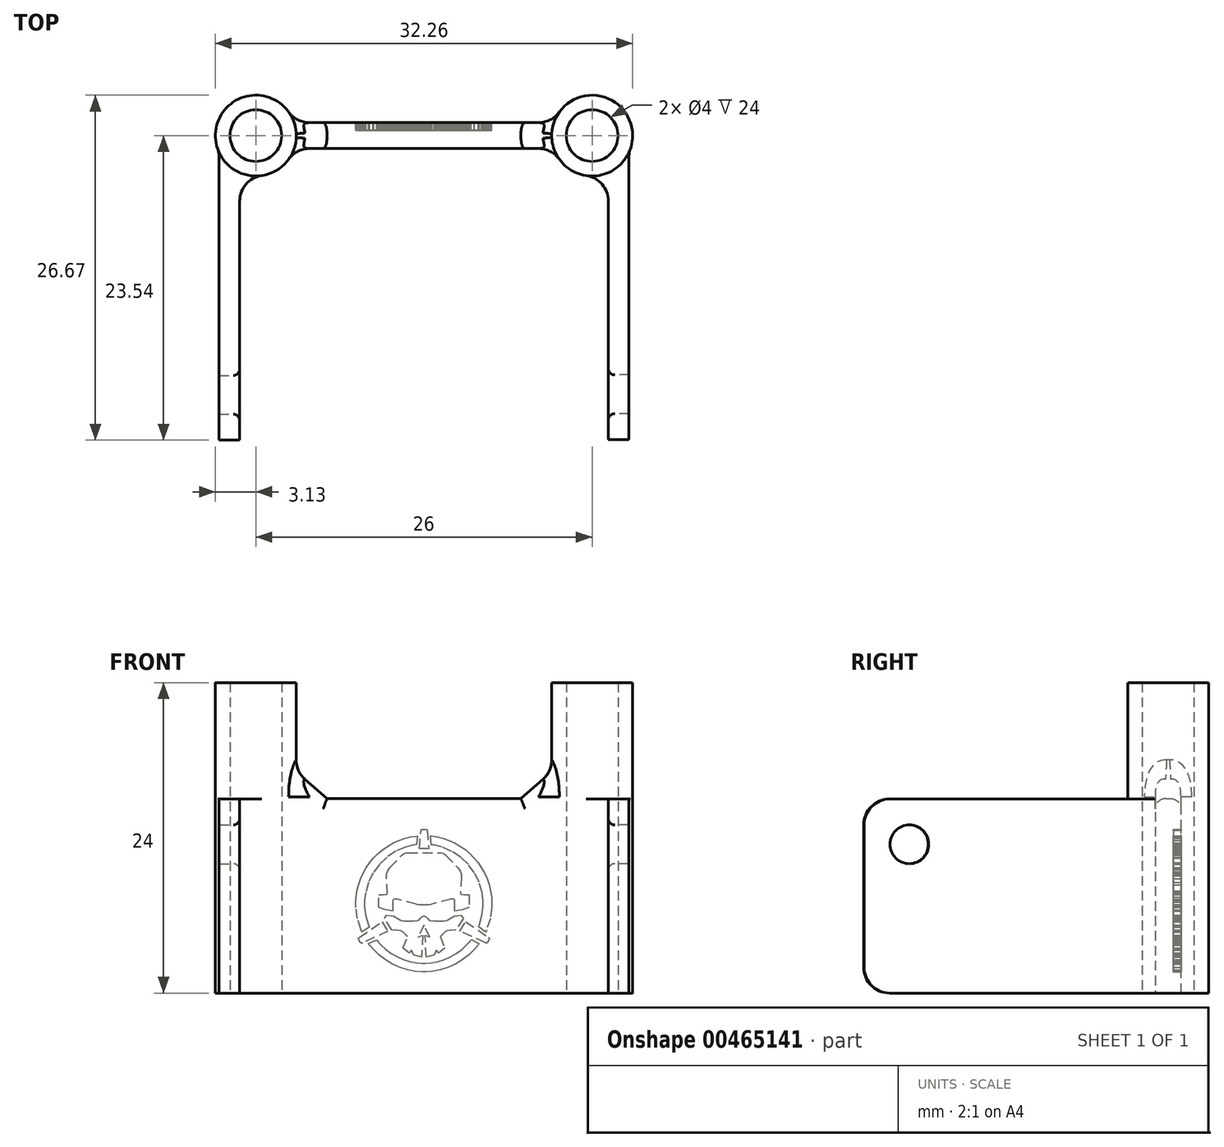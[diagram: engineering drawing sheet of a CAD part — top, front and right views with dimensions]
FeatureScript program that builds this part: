
annotation { "Feature Type Name" : "Feature", "Feature Type Description" : "" }
export const myFeature = defineFeature(function(context is Context, id is Id, definition is map)
    precondition{}
    {
        {
            var Q0;
            Q0=qCreatedBy(makeId("Top.planeOp"),FACE);
            var sketch = newSketch(context, id + "F0", { "sketchPlane" : qUnion([Q0])});
            skCircle(sketch, "E0", {"center": v(-13, 0) * mm, "radius": 3.12 * mm});
            skCircle(sketch, "E1", {"center": v(13, 0) * mm, "radius": 3.12 * mm});
            skSolve(sketch);
        }
        {
            var Q0;
            Q0 = qSketchRegion(id + "F0", true);
            extrude(context, id + "F1", {"entities" : qUnion([Q0]), "depth" : 24 * mm});
        }
        {
            var Q0;
            Q0=qCreatedBy(makeId("Front.planeOp"),FACE);
            var sketch = newSketch(context, id + "F2", { "sketchPlane" : qUnion([Q0])});
            skLineSegment(sketch, "E2", {"start": v(12, 0) * mm, "end": v(12, 19) * mm});
            skLineSegment(sketch, "E3", {"start": v(12, 19) * mm, "end": v(12, 19) * mm});
            skLineSegment(sketch, "E4", {"start": v(12, 19) * mm, "end": v(7.5, 15.03) * mm});
            skLineSegment(sketch, "E5", {"start": v(7.5, 15.03) * mm, "end": v(-7.5, 15.03) * mm});
            skLineSegment(sketch, "E6", {"start": v(-7.5, 15.03) * mm, "end": v(-12, 19) * mm});
            skLineSegment(sketch, "E7", {"start": v(-12, 19) * mm, "end": v(-12, 0) * mm});
            skLineSegment(sketch, "E8", {"start": v(-12, 0) * mm, "end": v(12, 0) * mm});
            skSolve(sketch);
        }
        {
            var Q0;
            Q0=makeQuery(id+"F2.imprint","IMPRINT",FACE,{"disambiguationData":[TD([[makeQuery(id+"F2.imprint","IMPRINT",EDGE,{"derivedFrom":sQuery(id+"F2.wireOp",EDGE,"E2")}),1.0]])]});
            extrude(context, id + "F3", {"entities" : qUnion([Q0]), "endBound" : BoundingType.SYMMETRIC, "depth" : 2 * mm});
        }
        {
            var Q0;
            Q0=qCreatedBy(makeId("Right.planeOp"),FACE);
            var Q1;
            Q1 = qBodyType(qCreatedBy(id + "F5" ,EDGE), BodyType.WIRE);
            cPlane(context, id + "F4", {"entities" : qUnion([Q0, Q1]), "cplaneType" : CPlaneType.OFFSET, "offset" : 14.25 * mm, "width" : 150 * mm, "height" : 150 * mm});
        }
        {
            var Q0;
            Q0=qCreatedBy(id+"F4.planeOp",FACE);
            var sketch = newSketch(context, id + "F5", { "sketchPlane" : qUnion([Q0])});
            skCircle(sketch, "E9", {"center": v(-20, 11.5) * mm, "radius": 1.5 * mm});
            skLineSegment(sketch, "E10", {"start": v(0, 0) * mm, "end": v(-21.5, 0) * mm});
            skLineSegment(sketch, "E11", {"start": v(-23.5, 2) * mm, "end": v(-23.5, 13) * mm});
            skLineSegment(sketch, "E12", {"start": v(-21.5, 15) * mm, "end": v(0, 15) * mm});
            skLineSegment(sketch, "E13", {"start": v(0, 15) * mm, "end": v(0, 0) * mm});
            skPoint(sketch, "E14.visualSharp", {"position": v(-23.5, 15) * mm});
            skArc(sketch, "E14.filletArc", {"start": v(-21.5, 15) * mm, "mid": v(-22.91, 14.41) * mm, "end": v(-23.5, 13) * mm});
            skPoint(sketch, "E15.visualSharp", {"position": v(-23.5, 0) * mm});
            skArc(sketch, "E15.filletArc", {"start": v(-23.5, 2) * mm, "mid": v(-22.91, 0.59) * mm, "end": v(-21.5, 0) * mm});
            skSolve(sketch);
        }
        {
            var Q0;
            Q0 = qSketchRegion(id + "F5", true);
            extrude(context, id + "F6", {"entities" : qUnion([Q0]), "operationType" : NewBodyOperationType.ADD, "depth" : 1.6 * mm});
        }
        {
            var Q0;
            Q0=qCreatedBy(makeId("Right.planeOp"),FACE);
            cPlane(context, id + "F7", {"entities" : qUnion([Q0]), "cplaneType" : CPlaneType.OFFSET, "offset" : 14.25 * mm, "oppositeDirection" : true, "width" : 150 * mm, "height" : 150 * mm});
        }
        {
            var Q0;
            Q0=qCreatedBy(id+"F7.planeOp",FACE);
            var sketch = newSketch(context, id + "F8", { "sketchPlane" : qUnion([Q0])});
            skCircle(sketch, "E16", {"center": v(-20.04, 11.5) * mm, "radius": 1.5 * mm});
            skLineSegment(sketch, "E17", {"start": v(-0.04, 0) * mm, "end": v(-21.54, 0) * mm});
            skLineSegment(sketch, "E18", {"start": v(-23.54, 2) * mm, "end": v(-23.54, 13) * mm});
            skLineSegment(sketch, "E19", {"start": v(-21.54, 15) * mm, "end": v(-0.04, 15) * mm});
            skLineSegment(sketch, "E20", {"start": v(-0.04, 15) * mm, "end": v(-0.04, 0) * mm});
            skPoint(sketch, "E21.visualSharp", {"position": v(-23.54, 15) * mm});
            skArc(sketch, "E21.filletArc", {"start": v(-21.54, 15) * mm, "mid": v(-22.95, 14.41) * mm, "end": v(-23.54, 13) * mm});
            skPoint(sketch, "E22.visualSharp", {"position": v(-23.54, 0) * mm});
            skArc(sketch, "E22.filletArc", {"start": v(-23.54, 2) * mm, "mid": v(-22.95, 0.59) * mm, "end": v(-21.54, 0) * mm});
            skSolve(sketch);
        }
        {
            var Q0;
            Q0 = qSketchRegion(id + "F8", true);
            extrude(context, id + "F9", {"entities" : qUnion([Q0]), "operationType" : NewBodyOperationType.ADD, "oppositeDirection" : true, "depth" : 1.6 * mm});
        }
        {
            var Q0;
            Q0=qCreatedBy(makeId("Top.planeOp"),FACE);
            var sketch = newSketch(context, id + "F10", { "sketchPlane" : qUnion([Q0])});
            skCircle(sketch, "E23", {"center": v(-13, 0) * mm, "radius": 0.5 * mm});
            skCircle(sketch, "E24", {"center": v(13, 0) * mm, "radius": 1.75 * mm});
            skSolve(sketch);
        }
        {
            var Q0;
            Q0=sQuery(id+"F10.wireOp",VERTEX,"E23.center");
            var Q1;
            Q1=sQuery(id+"F10.wireOp",VERTEX,"E24.center");
            var Q2;
            Q2=makeQuery(id+"F1.opExtrude","SWEPT_BODY",BODY,{"disambiguationData":[OSD([sQuery(id+"F0.wireOp",EDGE,"E0")])]});
            var Q3;
            Q3=makeQuery(id+"F3.opExtrude","SWEPT_BODY",BODY,{"disambiguationData":[OSD([sQuery(id+"F2.wireOp",EDGE,"in345Lub-D59E-tOme-60dj-Cq3KucnByxKd"),sQuery(id+"F2.wireOp",EDGE,"E2"),sQuery(id+"F2.wireOp",EDGE,"E4"),sQuery(id+"F2.wireOp",EDGE,"E5"),sQuery(id+"F2.wireOp",EDGE,"E6"),sQuery(id+"F2.wireOp",EDGE,"E7")])]});
            var Q4;
            Q4=makeQuery(id+"FYRTTrcSvXfLMjP_3.opExtrude","SWEPT_BODY",BODY,{"disambiguationData":[OSD([sQuery(id+"Fs8EBPNxBlUYa75_3.wireOp",EDGE,"JWLeMf17-8jiZ-tYXv-UtJK-ccR32AaEOkmf.bottom"),sQuery(id+"Fs8EBPNxBlUYa75_3.wireOp",EDGE,"JWLeMf17-8jiZ-tYXv-UtJK-ccR32AaEOkmf.top"),sQuery(id+"Fs8EBPNxBlUYa75_3.wireOp",EDGE,"JWLeMf17-8jiZ-tYXv-UtJK-ccR32AaEOkmf.left"),sQuery(id+"Fs8EBPNxBlUYa75_3.wireOp",EDGE,"JWLeMf17-8jiZ-tYXv-UtJK-ccR32AaEOkmf.right")])]});
            var Q5;
            Q5=makeQuery(id+"F1.opExtrude","SWEPT_BODY",BODY,{"disambiguationData":[OSD([sQuery(id+"F0.wireOp",EDGE,"E1")])]});
            var Q6;
            Q6=makeQuery(id+"FYRTTrcSvXfLMjP_3.opExtrude","SWEPT_BODY",BODY,{"disambiguationData":[OSD([sQuery(id+"Fs8EBPNxBlUYa75_3.wireOp",EDGE,"dHJZYZbQ-VqZX-6sAW-GdeU-ZCC2gI22Ho79.bottom"),sQuery(id+"Fs8EBPNxBlUYa75_3.wireOp",EDGE,"dHJZYZbQ-VqZX-6sAW-GdeU-ZCC2gI22Ho79.top"),sQuery(id+"Fs8EBPNxBlUYa75_3.wireOp",EDGE,"dHJZYZbQ-VqZX-6sAW-GdeU-ZCC2gI22Ho79.left"),sQuery(id+"Fs8EBPNxBlUYa75_3.wireOp",EDGE,"dHJZYZbQ-VqZX-6sAW-GdeU-ZCC2gI22Ho79.right")])]});
            hole(context, id + "F11", {"style" : HoleStyle.SIMPLE, "endStyle" : HoleEndStyle.THROUGH, "oppositeDirection" : true, "holeDiameter" : 4 * mm, "isTappedThrough" : true, "tappedDepth" : 12 * mm, "tapClearance" : 3, "locations" : qUnion([Q0, Q1]), "scope" : qUnion([Q2, Q3, Q4, Q5, Q6])});
        }
        {
            var Q0;
            Q0=makeQuery(id+"F1.opExtrude","SWEPT_BODY",BODY,{"disambiguationData":[OSD([sQuery(id+"F0.wireOp",EDGE,"E1")])]});
            var Q1;
            Q1=makeQuery(id+"F3.opExtrude","SWEPT_BODY",BODY,{"disambiguationData":[OSD([sQuery(id+"F2.wireOp",EDGE,"in345Lub-D59E-tOme-60dj-Cq3KucnByxKd"),sQuery(id+"F2.wireOp",EDGE,"E2"),sQuery(id+"F2.wireOp",EDGE,"E4"),sQuery(id+"F2.wireOp",EDGE,"E5"),sQuery(id+"F2.wireOp",EDGE,"E6"),sQuery(id+"F2.wireOp",EDGE,"E7")])]});
            var Q2;
            Q2=makeQuery(id+"F1.opExtrude","SWEPT_BODY",BODY,{"disambiguationData":[OSD([sQuery(id+"F0.wireOp",EDGE,"E0")])]});
            booleanBodies(context, id + "F12", {"operationType" : BooleanOperationType.UNION, "tools" : qUnion([Q0, Q1, Q2])});
        }
        {
            var Q0;
            Q0=makeQuery(id+"F3.opExtrude","CAP_EDGE",EDGE,{"disambiguationData":[OSD([sQuery(id+"F2.wireOp",EDGE,"E5")])],"isStart":false});
            var Q1;
            Q1=makeQuery(id+"F3.opExtrude","CAP_EDGE",EDGE,{"disambiguationData":[OSD([sQuery(id+"F2.wireOp",EDGE,"E5")])],"isStart":true});
            var Q2;
            Q2=makeQuery(id+"F3.opExtrude","CAP_EDGE",EDGE,{"disambiguationData":[OSD([sQuery(id+"F2.wireOp",EDGE,"E6")])],"isStart":false});
            var Q3;
            Q3=makeQuery(id+"F3.opExtrude","CAP_EDGE",EDGE,{"disambiguationData":[OSD([sQuery(id+"F2.wireOp",EDGE,"E6")])],"isStart":true});
            var Q4;
            Q4=makeQuery(id+"F3.opExtrude","CAP_EDGE",EDGE,{"disambiguationData":[OSD([sQuery(id+"F2.wireOp",EDGE,"E4")])],"isStart":false});
            var Q5;
            Q5=makeQuery(id+"F3.opExtrude","CAP_EDGE",EDGE,{"disambiguationData":[OSD([sQuery(id+"F2.wireOp",EDGE,"E4")])],"isStart":true});
            fillet(context, id + "F13", {"entities" : qUnion([Q0, Q1, Q2, Q3, Q4, Q5]), "radius" : .8 * mm, "tangentPropagation" : true, "allowEdgeOverflow" : false});
        }
        {
            var Q0;
            Q0=makeQuery(id+"F11.hole-0.boolean.opBoolean","INTERSECT",EDGE,{"derivedFrom":[makeQuery(id+"F1.opExtrude","CAP_FACE",FACE,{"disambiguationData":[OSD([sQuery(id+"F0.wireOp",EDGE,"E0")])],"isStart":false}),makeQuery(id+"F11.hole-0.opRevolve","SWEPT_FACE",FACE,{"disambiguationData":[OSD([sQuery(id+"F11.hole-0.sketch.wireOp",EDGE,"core_line_2")])]})]});
            var Q1;
            Q1=makeQuery(id+"F11.hole-1.boolean.opBoolean","INTERSECT",EDGE,{"derivedFrom":[makeQuery(id+"F1.opExtrude","CAP_FACE",FACE,{"disambiguationData":[OSD([sQuery(id+"F0.wireOp",EDGE,"E1")])],"isStart":false}),makeQuery(id+"F11.hole-1.opRevolve","SWEPT_FACE",FACE,{"disambiguationData":[OSD([sQuery(id+"F11.hole-1.sketch.wireOp",EDGE,"core_line_2")])]})]});
            var Q2;
            Q2=makeQuery(id+"F9.opExtrude","CAP_EDGE",EDGE,{"disambiguationData":[OSD([sQuery(id+"F8.wireOp",EDGE,"E16")])],"isStart":true});
            var Q3;
            Q3=makeQuery(id+"F6.opExtrude","CAP_EDGE",EDGE,{"disambiguationData":[OSD([sQuery(id+"F5.wireOp",EDGE,"E9")])],"isStart":true});
            fillet(context, id + "F14", {"entities" : qUnion([Q0, Q1, Q2, Q3]), "radius" : .5 * mm, "tangentPropagation" : true, "allowEdgeOverflow" : false});
        }
        {
            var Q0;
            Q0=makeQuery(id+"F3.opExtrude","CAP_FACE",FACE,{"disambiguationData":[OSD([sQuery(id+"F2.wireOp",EDGE,"E2"),sQuery(id+"F2.wireOp",EDGE,"E4"),sQuery(id+"F2.wireOp",EDGE,"E5"),sQuery(id+"F2.wireOp",EDGE,"E6"),sQuery(id+"F2.wireOp",EDGE,"E7"),sQuery(id+"F2.wireOp",EDGE,"E8")])],"isStart":true});
            var sketch = newSketch(context, id + "F15", { "sketchPlane" : qUnion([Q0])});
            skLineSegment(sketch, "E25", {"start": v(-0.2, 12.65) * mm, "end": v(-0.2, 12.64) * mm});
            skLineSegment(sketch, "E26", {"start": v(-0.2, 12.64) * mm, "end": v(-0.23, 12.63) * mm});
            skLineSegment(sketch, "E27", {"start": v(-0.23, 12.63) * mm, "end": v(-0.24, 12.59) * mm});
            skLineSegment(sketch, "E28", {"start": v(-0.24, 12.59) * mm, "end": v(-0.24, 12.58) * mm});
            skLineSegment(sketch, "E29", {"start": v(-0.24, 12.58) * mm, "end": v(-0.38, 11.17) * mm});
            skLineSegment(sketch, "E30", {"start": v(-0.38, 11.17) * mm, "end": v(0.36, 11.17) * mm});
            skLineSegment(sketch, "E31", {"start": v(0.36, 11.17) * mm, "end": v(0.22, 12.58) * mm});
            skLineSegment(sketch, "E32", {"start": v(0.22, 12.58) * mm, "end": v(0.22, 12.59) * mm});
            skLineSegment(sketch, "E33", {"start": v(0.22, 12.59) * mm, "end": v(0.2, 12.63) * mm});
            skLineSegment(sketch, "E34", {"start": v(0.2, 12.63) * mm, "end": v(0.19, 12.64) * mm});
            skLineSegment(sketch, "E35", {"start": v(0.19, 12.64) * mm, "end": v(0.18, 12.65) * mm});
            skLineSegment(sketch, "E36", {"start": v(0.18, 12.65) * mm, "end": v(-0.2, 12.65) * mm});
            skLineSegment(sketch, "E37", {"start": v(-0.5, 12.15) * mm, "end": v(-0.63, 12.13) * mm});
            skLineSegment(sketch, "E38", {"start": v(-0.63, 12.13) * mm, "end": v(-1, 12.07) * mm});
            skLineSegment(sketch, "E39", {"start": v(-1, 12.07) * mm, "end": v(-1.48, 11.96) * mm});
            skLineSegment(sketch, "E40", {"start": v(-1.48, 11.96) * mm, "end": v(-1.94, 11.8) * mm});
            skLineSegment(sketch, "E41", {"start": v(-1.94, 11.8) * mm, "end": v(-2.38, 11.6) * mm});
            skLineSegment(sketch, "E42", {"start": v(-2.38, 11.6) * mm, "end": v(-2.8, 11.36) * mm});
            skLineSegment(sketch, "E43", {"start": v(-2.8, 11.36) * mm, "end": v(-3.19, 11.09) * mm});
            skLineSegment(sketch, "E44", {"start": v(-3.19, 11.09) * mm, "end": v(-3.55, 10.78) * mm});
            skLineSegment(sketch, "E45", {"start": v(-3.55, 10.78) * mm, "end": v(-3.89, 10.44) * mm});
            skLineSegment(sketch, "E46", {"start": v(-3.89, 10.44) * mm, "end": v(-4.19, 10.08) * mm});
            skLineSegment(sketch, "E47", {"start": v(-4.19, 10.08) * mm, "end": v(-4.46, 9.69) * mm});
            skLineSegment(sketch, "E48", {"start": v(-4.46, 9.69) * mm, "end": v(-4.69, 9.27) * mm});
            skLineSegment(sketch, "E49", {"start": v(-4.69, 9.27) * mm, "end": v(-4.88, 8.83) * mm});
            skLineSegment(sketch, "E50", {"start": v(-4.88, 8.83) * mm, "end": v(-5.04, 8.38) * mm});
            skLineSegment(sketch, "E51", {"start": v(-5.04, 8.38) * mm, "end": v(-5.15, 7.9) * mm});
            skLineSegment(sketch, "E52", {"start": v(-5.15, 7.9) * mm, "end": v(-5.22, 7.41) * mm});
            skLineSegment(sketch, "E53", {"start": v(-5.22, 7.41) * mm, "end": v(-5.25, 7.04) * mm});
            skLineSegment(sketch, "E54", {"start": v(-5.25, 7.04) * mm, "end": v(-5.25, 6.9) * mm});
            skLineSegment(sketch, "E55", {"start": v(-5.25, 6.9) * mm, "end": v(-5.25, 6.63) * mm});
            skLineSegment(sketch, "E56", {"start": v(-5.25, 6.63) * mm, "end": v(-5.12, 5.77) * mm});
            skLineSegment(sketch, "E57", {"start": v(-5.12, 5.77) * mm, "end": v(-4.85, 4.89) * mm});
            skLineSegment(sketch, "E58", {"start": v(-4.85, 4.89) * mm, "end": v(-4.77, 4.72) * mm});
            skLineSegment(sketch, "E59", {"start": v(-4.77, 4.72) * mm, "end": v(-4.22, 5.12) * mm});
            skLineSegment(sketch, "E60", {"start": v(-4.22, 5.12) * mm, "end": v(-4.28, 5.25) * mm});
            skLineSegment(sketch, "E61", {"start": v(-4.28, 5.25) * mm, "end": v(-4.49, 5.98) * mm});
            skLineSegment(sketch, "E62", {"start": v(-4.49, 5.98) * mm, "end": v(-4.58, 6.68) * mm});
            skLineSegment(sketch, "E63", {"start": v(-4.58, 6.68) * mm, "end": v(-4.58, 6.9) * mm});
            skLineSegment(sketch, "E64", {"start": v(-4.58, 6.9) * mm, "end": v(-4.58, 7.12) * mm});
            skLineSegment(sketch, "E65", {"start": v(-4.58, 7.12) * mm, "end": v(-4.5, 7.76) * mm});
            skLineSegment(sketch, "E66", {"start": v(-4.5, 7.76) * mm, "end": v(-4.28, 8.56) * mm});
            skLineSegment(sketch, "E67", {"start": v(-4.28, 8.56) * mm, "end": v(-3.91, 9.3) * mm});
            skLineSegment(sketch, "E68", {"start": v(-3.91, 9.3) * mm, "end": v(-3.43, 9.95) * mm});
            skLineSegment(sketch, "E69", {"start": v(-3.43, 9.95) * mm, "end": v(-2.84, 10.5) * mm});
            skLineSegment(sketch, "E70", {"start": v(-2.84, 10.5) * mm, "end": v(-2.16, 10.96) * mm});
            skLineSegment(sketch, "E71", {"start": v(-2.16, 10.96) * mm, "end": v(-1.4, 11.28) * mm});
            skLineSegment(sketch, "E72", {"start": v(-1.4, 11.28) * mm, "end": v(-0.78, 11.44) * mm});
            skLineSegment(sketch, "E73", {"start": v(-0.78, 11.44) * mm, "end": v(-0.57, 11.46) * mm});
            skLineSegment(sketch, "E74", {"start": v(-0.57, 11.46) * mm, "end": v(-0.5, 12.15) * mm});
            skLineSegment(sketch, "E75", {"start": v(0.52, 12.14) * mm, "end": v(0.58, 11.47) * mm});
            skLineSegment(sketch, "E76", {"start": v(0.58, 11.47) * mm, "end": v(0.79, 11.44) * mm});
            skLineSegment(sketch, "E77", {"start": v(0.79, 11.44) * mm, "end": v(1.4, 11.28) * mm});
            skLineSegment(sketch, "E78", {"start": v(1.4, 11.28) * mm, "end": v(2.17, 10.96) * mm});
            skLineSegment(sketch, "E79", {"start": v(2.17, 10.96) * mm, "end": v(2.86, 10.5) * mm});
            skLineSegment(sketch, "E80", {"start": v(2.86, 10.5) * mm, "end": v(3.45, 9.95) * mm});
            skLineSegment(sketch, "E81", {"start": v(3.45, 9.95) * mm, "end": v(3.93, 9.3) * mm});
            skLineSegment(sketch, "E82", {"start": v(3.93, 9.3) * mm, "end": v(4.3, 8.56) * mm});
            skLineSegment(sketch, "E83", {"start": v(4.3, 8.56) * mm, "end": v(4.52, 7.76) * mm});
            skLineSegment(sketch, "E84", {"start": v(4.52, 7.76) * mm, "end": v(4.6, 7.12) * mm});
            skLineSegment(sketch, "E85", {"start": v(4.6, 7.12) * mm, "end": v(4.6, 6.9) * mm});
            skLineSegment(sketch, "E86", {"start": v(4.6, 6.9) * mm, "end": v(4.6, 6.68) * mm});
            skLineSegment(sketch, "E87", {"start": v(4.6, 6.68) * mm, "end": v(4.5, 5.98) * mm});
            skLineSegment(sketch, "E88", {"start": v(4.5, 5.98) * mm, "end": v(4.3, 5.25) * mm});
            skLineSegment(sketch, "E89", {"start": v(4.3, 5.25) * mm, "end": v(4.23, 5.11) * mm});
            skLineSegment(sketch, "E90", {"start": v(4.23, 5.11) * mm, "end": v(4.78, 4.71) * mm});
            skLineSegment(sketch, "E91", {"start": v(4.78, 4.71) * mm, "end": v(4.86, 4.88) * mm});
            skLineSegment(sketch, "E92", {"start": v(4.86, 4.88) * mm, "end": v(5.14, 5.77) * mm});
            skLineSegment(sketch, "E93", {"start": v(5.14, 5.77) * mm, "end": v(5.26, 6.62) * mm});
            skLineSegment(sketch, "E94", {"start": v(5.26, 6.62) * mm, "end": v(5.26, 6.9) * mm});
            skLineSegment(sketch, "E95", {"start": v(5.26, 6.9) * mm, "end": v(5.26, 7.04) * mm});
            skLineSegment(sketch, "E96", {"start": v(5.26, 7.04) * mm, "end": v(5.24, 7.41) * mm});
            skLineSegment(sketch, "E97", {"start": v(5.24, 7.41) * mm, "end": v(5.17, 7.9) * mm});
            skLineSegment(sketch, "E98", {"start": v(5.17, 7.9) * mm, "end": v(5.05, 8.37) * mm});
            skLineSegment(sketch, "E99", {"start": v(5.05, 8.37) * mm, "end": v(4.9, 8.83) * mm});
            skLineSegment(sketch, "E100", {"start": v(4.9, 8.83) * mm, "end": v(4.7, 9.27) * mm});
            skLineSegment(sketch, "E101", {"start": v(4.7, 9.27) * mm, "end": v(4.47, 9.68) * mm});
            skLineSegment(sketch, "E102", {"start": v(4.47, 9.68) * mm, "end": v(4.2, 10.08) * mm});
            skLineSegment(sketch, "E103", {"start": v(4.2, 10.08) * mm, "end": v(3.9, 10.44) * mm});
            skLineSegment(sketch, "E104", {"start": v(3.9, 10.44) * mm, "end": v(3.56, 10.78) * mm});
            skLineSegment(sketch, "E105", {"start": v(3.56, 10.78) * mm, "end": v(3.2, 11.08) * mm});
            skLineSegment(sketch, "E106", {"start": v(3.2, 11.08) * mm, "end": v(2.8, 11.36) * mm});
            skLineSegment(sketch, "E107", {"start": v(2.8, 11.36) * mm, "end": v(2.4, 11.6) * mm});
            skLineSegment(sketch, "E108", {"start": v(2.4, 11.6) * mm, "end": v(1.95, 11.8) * mm});
            skLineSegment(sketch, "E109", {"start": v(1.95, 11.8) * mm, "end": v(1.5, 11.95) * mm});
            skLineSegment(sketch, "E110", {"start": v(1.5, 11.95) * mm, "end": v(1.01, 12.07) * mm});
            skLineSegment(sketch, "E111", {"start": v(1.01, 12.07) * mm, "end": v(0.64, 12.13) * mm});
            skLineSegment(sketch, "E112", {"start": v(0.64, 12.13) * mm, "end": v(0.52, 12.14) * mm});
            skLineSegment(sketch, "E113", {"start": v(-1.2, 10.86) * mm, "end": v(-1.23, 10.86) * mm});
            skLineSegment(sketch, "E114", {"start": v(-1.23, 10.86) * mm, "end": v(-1.34, 10.84) * mm});
            skLineSegment(sketch, "E115", {"start": v(-1.34, 10.84) * mm, "end": v(-1.47, 10.8) * mm});
            skLineSegment(sketch, "E116", {"start": v(-1.47, 10.8) * mm, "end": v(-1.59, 10.75) * mm});
            skLineSegment(sketch, "E117", {"start": v(-1.59, 10.75) * mm, "end": v(-1.66, 10.69) * mm});
            skLineSegment(sketch, "E118", {"start": v(-1.66, 10.69) * mm, "end": v(-1.69, 10.66) * mm});
            skLineSegment(sketch, "E119", {"start": v(-1.69, 10.66) * mm, "end": v(-2.61, 9.7) * mm});
            skLineSegment(sketch, "E120", {"start": v(-2.61, 9.7) * mm, "end": v(-2.64, 9.67) * mm});
            skLineSegment(sketch, "E121", {"start": v(-2.64, 9.67) * mm, "end": v(-2.72, 9.56) * mm});
            skLineSegment(sketch, "E122", {"start": v(-2.72, 9.56) * mm, "end": v(-2.81, 9.39) * mm});
            skLineSegment(sketch, "E123", {"start": v(-2.81, 9.39) * mm, "end": v(-2.87, 9.2) * mm});
            skLineSegment(sketch, "E124", {"start": v(-2.87, 9.2) * mm, "end": v(-2.9, 9.05) * mm});
            skLineSegment(sketch, "E125", {"start": v(-2.9, 9.05) * mm, "end": v(-2.9, 9) * mm});
            skLineSegment(sketch, "E126", {"start": v(-2.9, 9) * mm, "end": v(-2.82, 7.67) * mm});
            skLineSegment(sketch, "E127", {"start": v(-2.82, 7.67) * mm, "end": v(-2.87, 7.65) * mm});
            skLineSegment(sketch, "E128", {"start": v(-2.87, 7.65) * mm, "end": v(-3.14, 7.6) * mm});
            skLineSegment(sketch, "E129", {"start": v(-3.14, 7.6) * mm, "end": v(-3.42, 7.6) * mm});
            skLineSegment(sketch, "E130", {"start": v(-3.42, 7.6) * mm, "end": v(-3.48, 7.6) * mm});
            skLineSegment(sketch, "E131", {"start": v(-3.48, 7.6) * mm, "end": v(-3.48, 6.61) * mm});
            skLineSegment(sketch, "E132", {"start": v(-3.48, 6.61) * mm, "end": v(-2.94, 6.42) * mm});
            skLineSegment(sketch, "E133", {"start": v(-2.94, 6.42) * mm, "end": v(-2.4, 6.35) * mm});
            skLineSegment(sketch, "E134", {"start": v(-2.4, 6.35) * mm, "end": v(-2.4, 7.11) * mm});
            skLineSegment(sketch, "E135", {"start": v(-2.4, 7.11) * mm, "end": v(-2.4, 7.13) * mm});
            skLineSegment(sketch, "E136", {"start": v(-2.4, 7.13) * mm, "end": v(-2.37, 7.2) * mm});
            skLineSegment(sketch, "E137", {"start": v(-2.37, 7.2) * mm, "end": v(-2.31, 7.25) * mm});
            skLineSegment(sketch, "E138", {"start": v(-2.31, 7.25) * mm, "end": v(-2.21, 7.27) * mm});
            skLineSegment(sketch, "E139", {"start": v(-2.21, 7.27) * mm, "end": v(-2.1, 7.27) * mm});
            skLineSegment(sketch, "E140", {"start": v(-2.1, 7.27) * mm, "end": v(-2.07, 7.26) * mm});
            skLineSegment(sketch, "E141", {"start": v(-2.07, 7.26) * mm, "end": v(-0.6, 6.87) * mm});
            skLineSegment(sketch, "E142", {"start": v(-0.6, 6.87) * mm, "end": v(-0.57, 6.86) * mm});
            skLineSegment(sketch, "E143", {"start": v(-0.57, 6.86) * mm, "end": v(-0.4, 6.82) * mm});
            skLineSegment(sketch, "E144", {"start": v(-0.4, 6.82) * mm, "end": v(-0.27, 6.8) * mm});
            skLineSegment(sketch, "E145", {"start": v(-0.27, 6.8) * mm, "end": v(-0.23, 6.8) * mm});
            skLineSegment(sketch, "E146", {"start": v(-0.23, 6.8) * mm, "end": v(0.24, 6.8) * mm});
            skLineSegment(sketch, "E147", {"start": v(0.24, 6.8) * mm, "end": v(0.29, 6.8) * mm});
            skLineSegment(sketch, "E148", {"start": v(0.29, 6.8) * mm, "end": v(0.42, 6.82) * mm});
            skLineSegment(sketch, "E149", {"start": v(0.42, 6.82) * mm, "end": v(0.58, 6.86) * mm});
            skLineSegment(sketch, "E150", {"start": v(0.58, 6.86) * mm, "end": v(0.61, 6.87) * mm});
            skLineSegment(sketch, "E151", {"start": v(0.61, 6.87) * mm, "end": v(2.08, 7.26) * mm});
            skLineSegment(sketch, "E152", {"start": v(2.08, 7.26) * mm, "end": v(2.12, 7.27) * mm});
            skLineSegment(sketch, "E153", {"start": v(2.12, 7.27) * mm, "end": v(2.23, 7.27) * mm});
            skLineSegment(sketch, "E154", {"start": v(2.23, 7.27) * mm, "end": v(2.33, 7.25) * mm});
            skLineSegment(sketch, "E155", {"start": v(2.33, 7.25) * mm, "end": v(2.39, 7.2) * mm});
            skLineSegment(sketch, "E156", {"start": v(2.39, 7.2) * mm, "end": v(2.4, 7.13) * mm});
            skLineSegment(sketch, "E157", {"start": v(2.4, 7.13) * mm, "end": v(2.4, 7.11) * mm});
            skLineSegment(sketch, "E158", {"start": v(2.4, 7.11) * mm, "end": v(2.4, 6.35) * mm});
            skLineSegment(sketch, "E159", {"start": v(2.4, 6.35) * mm, "end": v(2.96, 6.42) * mm});
            skLineSegment(sketch, "E160", {"start": v(2.96, 6.42) * mm, "end": v(3.5, 6.61) * mm});
            skLineSegment(sketch, "E161", {"start": v(3.5, 6.61) * mm, "end": v(3.5, 7.6) * mm});
            skLineSegment(sketch, "E162", {"start": v(3.5, 7.6) * mm, "end": v(3.44, 7.6) * mm});
            skLineSegment(sketch, "E163", {"start": v(3.44, 7.6) * mm, "end": v(3.16, 7.6) * mm});
            skLineSegment(sketch, "E164", {"start": v(3.16, 7.6) * mm, "end": v(2.89, 7.65) * mm});
            skLineSegment(sketch, "E165", {"start": v(2.89, 7.65) * mm, "end": v(2.84, 7.67) * mm});
            skLineSegment(sketch, "E166", {"start": v(2.84, 7.67) * mm, "end": v(2.9, 9) * mm});
            skLineSegment(sketch, "E167", {"start": v(2.9, 9) * mm, "end": v(2.9, 9.05) * mm});
            skLineSegment(sketch, "E168", {"start": v(2.9, 9.05) * mm, "end": v(2.89, 9.2) * mm});
            skLineSegment(sketch, "E169", {"start": v(2.89, 9.2) * mm, "end": v(2.83, 9.39) * mm});
            skLineSegment(sketch, "E170", {"start": v(2.83, 9.39) * mm, "end": v(2.73, 9.56) * mm});
            skLineSegment(sketch, "E171", {"start": v(2.73, 9.56) * mm, "end": v(2.66, 9.67) * mm});
            skLineSegment(sketch, "E172", {"start": v(2.66, 9.67) * mm, "end": v(2.63, 9.7) * mm});
            skLineSegment(sketch, "E173", {"start": v(2.63, 9.7) * mm, "end": v(1.7, 10.66) * mm});
            skLineSegment(sketch, "E174", {"start": v(1.7, 10.66) * mm, "end": v(1.68, 10.69) * mm});
            skLineSegment(sketch, "E175", {"start": v(1.68, 10.69) * mm, "end": v(1.6, 10.75) * mm});
            skLineSegment(sketch, "E176", {"start": v(1.6, 10.75) * mm, "end": v(1.49, 10.8) * mm});
            skLineSegment(sketch, "E177", {"start": v(1.49, 10.8) * mm, "end": v(1.36, 10.84) * mm});
            skLineSegment(sketch, "E178", {"start": v(1.36, 10.84) * mm, "end": v(1.24, 10.86) * mm});
            skLineSegment(sketch, "E179", {"start": v(1.24, 10.86) * mm, "end": v(1.2, 10.86) * mm});
            skLineSegment(sketch, "E180", {"start": v(1.2, 10.86) * mm, "end": v(-1.2, 10.86) * mm});
            skLineSegment(sketch, "E181", {"start": v(-2.87, 6.03) * mm, "end": v(-3.04, 5.77) * mm});
            skLineSegment(sketch, "E182", {"start": v(-3.04, 5.77) * mm, "end": v(-2.46, 4.87) * mm});
            skLineSegment(sketch, "E183", {"start": v(-2.46, 4.87) * mm, "end": v(-2.05, 4.85) * mm});
            skLineSegment(sketch, "E184", {"start": v(-2.05, 4.85) * mm, "end": v(-2, 4.85) * mm});
            skLineSegment(sketch, "E185", {"start": v(-2, 4.85) * mm, "end": v(-1.8, 4.83) * mm});
            skLineSegment(sketch, "E186", {"start": v(-1.8, 4.83) * mm, "end": v(-1.63, 4.76) * mm});
            skLineSegment(sketch, "E187", {"start": v(-1.63, 4.76) * mm, "end": v(-1.6, 4.73) * mm});
            skLineSegment(sketch, "E188", {"start": v(-1.6, 4.73) * mm, "end": v(-1.26, 4.38) * mm});
            skLineSegment(sketch, "E189", {"start": v(-1.26, 4.38) * mm, "end": v(-1.61, 3.48) * mm});
            skLineSegment(sketch, "E190", {"start": v(-1.61, 3.48) * mm, "end": v(-1.14, 3.1) * mm});
            skLineSegment(sketch, "E191", {"start": v(-1.14, 3.1) * mm, "end": v(-0.94, 3.31) * mm});
            skLineSegment(sketch, "E192", {"start": v(-0.94, 3.31) * mm, "end": v(-0.78, 2.93) * mm});
            skLineSegment(sketch, "E193", {"start": v(-0.78, 2.93) * mm, "end": v(-0.18, 2.77) * mm});
            skLineSegment(sketch, "E194", {"start": v(-0.18, 2.77) * mm, "end": v(-0.08, 4.48) * mm});
            skLineSegment(sketch, "E195", {"start": v(-0.08, 4.48) * mm, "end": v(-0.43, 4.33) * mm});
            skLineSegment(sketch, "E196", {"start": v(-0.43, 4.33) * mm, "end": v(0, 5.26) * mm});
            skLineSegment(sketch, "E197", {"start": v(0, 5.26) * mm, "end": v(0.45, 4.33) * mm});
            skLineSegment(sketch, "E198", {"start": v(0.45, 4.33) * mm, "end": v(0.1, 4.48) * mm});
            skLineSegment(sketch, "E199", {"start": v(0.1, 4.48) * mm, "end": v(0.2, 2.77) * mm});
            skLineSegment(sketch, "E200", {"start": v(0.2, 2.77) * mm, "end": v(0.8, 2.93) * mm});
            skLineSegment(sketch, "E201", {"start": v(0.8, 2.93) * mm, "end": v(0.95, 3.31) * mm});
            skLineSegment(sketch, "E202", {"start": v(0.95, 3.31) * mm, "end": v(1.15, 3.1) * mm});
            skLineSegment(sketch, "E203", {"start": v(1.15, 3.1) * mm, "end": v(1.63, 3.48) * mm});
            skLineSegment(sketch, "E204", {"start": v(1.63, 3.48) * mm, "end": v(1.27, 4.38) * mm});
            skLineSegment(sketch, "E205", {"start": v(1.27, 4.38) * mm, "end": v(1.62, 4.73) * mm});
            skLineSegment(sketch, "E206", {"start": v(1.62, 4.73) * mm, "end": v(1.65, 4.76) * mm});
            skLineSegment(sketch, "E207", {"start": v(1.65, 4.76) * mm, "end": v(1.82, 4.83) * mm});
            skLineSegment(sketch, "E208", {"start": v(1.82, 4.83) * mm, "end": v(2.02, 4.85) * mm});
            skLineSegment(sketch, "E209", {"start": v(2.02, 4.85) * mm, "end": v(2.07, 4.85) * mm});
            skLineSegment(sketch, "E210", {"start": v(2.07, 4.85) * mm, "end": v(2.48, 4.87) * mm});
            skLineSegment(sketch, "E211", {"start": v(2.48, 4.87) * mm, "end": v(3.06, 5.77) * mm});
            skLineSegment(sketch, "E212", {"start": v(3.06, 5.77) * mm, "end": v(2.88, 6.03) * mm});
            skLineSegment(sketch, "E213", {"start": v(2.88, 6.03) * mm, "end": v(2.35, 5.97) * mm});
            skLineSegment(sketch, "E214", {"start": v(2.35, 5.97) * mm, "end": v(1.82, 5.64) * mm});
            skLineSegment(sketch, "E215", {"start": v(1.82, 5.64) * mm, "end": v(1.75, 5.62) * mm});
            skLineSegment(sketch, "E216", {"start": v(1.75, 5.62) * mm, "end": v(1.53, 5.59) * mm});
            skLineSegment(sketch, "E217", {"start": v(1.53, 5.59) * mm, "end": v(1.2, 5.57) * mm});
            skLineSegment(sketch, "E218", {"start": v(1.2, 5.57) * mm, "end": v(0.83, 5.58) * mm});
            skLineSegment(sketch, "E219", {"start": v(0.83, 5.58) * mm, "end": v(0.5, 5.61) * mm});
            skLineSegment(sketch, "E220", {"start": v(0.5, 5.61) * mm, "end": v(0.4, 5.63) * mm});
            skLineSegment(sketch, "E221", {"start": v(0.4, 5.63) * mm, "end": v(0.38, 5.65) * mm});
            skLineSegment(sketch, "E222", {"start": v(0.38, 5.65) * mm, "end": v(0.33, 5.73) * mm});
            skLineSegment(sketch, "E223", {"start": v(0.33, 5.73) * mm, "end": v(0.23, 5.84) * mm});
            skLineSegment(sketch, "E224", {"start": v(0.23, 5.84) * mm, "end": v(0.12, 5.93) * mm});
            skLineSegment(sketch, "E225", {"start": v(0.12, 5.93) * mm, "end": v(0.04, 5.96) * mm});
            skLineSegment(sketch, "E226", {"start": v(0.04, 5.96) * mm, "end": v(0, 5.96) * mm});
            skLineSegment(sketch, "E227", {"start": v(0, 5.96) * mm, "end": v(-0.02, 5.96) * mm});
            skLineSegment(sketch, "E228", {"start": v(-0.02, 5.96) * mm, "end": v(-0.1, 5.93) * mm});
            skLineSegment(sketch, "E229", {"start": v(-0.1, 5.93) * mm, "end": v(-0.22, 5.84) * mm});
            skLineSegment(sketch, "E230", {"start": v(-0.22, 5.84) * mm, "end": v(-0.31, 5.73) * mm});
            skLineSegment(sketch, "E231", {"start": v(-0.31, 5.73) * mm, "end": v(-0.36, 5.65) * mm});
            skLineSegment(sketch, "E232", {"start": v(-0.36, 5.65) * mm, "end": v(-0.38, 5.63) * mm});
            skLineSegment(sketch, "E233", {"start": v(-0.38, 5.63) * mm, "end": v(-0.49, 5.61) * mm});
            skLineSegment(sketch, "E234", {"start": v(-0.49, 5.61) * mm, "end": v(-0.81, 5.58) * mm});
            skLineSegment(sketch, "E235", {"start": v(-0.81, 5.58) * mm, "end": v(-1.19, 5.57) * mm});
            skLineSegment(sketch, "E236", {"start": v(-1.19, 5.57) * mm, "end": v(-1.52, 5.59) * mm});
            skLineSegment(sketch, "E237", {"start": v(-1.52, 5.59) * mm, "end": v(-1.73, 5.62) * mm});
            skLineSegment(sketch, "E238", {"start": v(-1.73, 5.62) * mm, "end": v(-1.8, 5.64) * mm});
            skLineSegment(sketch, "E239", {"start": v(-1.8, 5.64) * mm, "end": v(-2.34, 5.97) * mm});
            skLineSegment(sketch, "E240", {"start": v(-2.34, 5.97) * mm, "end": v(-2.87, 6.03) * mm});
            skLineSegment(sketch, "E241", {"start": v(-3.23, 5.53) * mm, "end": v(-4.99, 4.3) * mm});
            skLineSegment(sketch, "E242", {"start": v(-4.99, 4.3) * mm, "end": v(-5, 4.28) * mm});
            skLineSegment(sketch, "E243", {"start": v(-5, 4.28) * mm, "end": v(-5.05, 4.24) * mm});
            skLineSegment(sketch, "E244", {"start": v(-5.05, 4.24) * mm, "end": v(-5.06, 4.2) * mm});
            skLineSegment(sketch, "E245", {"start": v(-5.06, 4.2) * mm, "end": v(-5.06, 4.2) * mm});
            skLineSegment(sketch, "E246", {"start": v(-5.06, 4.2) * mm, "end": v(-4.87, 3.86) * mm});
            skLineSegment(sketch, "E247", {"start": v(-4.87, 3.86) * mm, "end": v(-4.86, 3.86) * mm});
            skLineSegment(sketch, "E248", {"start": v(-4.86, 3.86) * mm, "end": v(-4.82, 3.85) * mm});
            skLineSegment(sketch, "E249", {"start": v(-4.82, 3.85) * mm, "end": v(-4.77, 3.87) * mm});
            skLineSegment(sketch, "E250", {"start": v(-4.77, 3.87) * mm, "end": v(-4.75, 3.88) * mm});
            skLineSegment(sketch, "E251", {"start": v(-4.75, 3.88) * mm, "end": v(-2.77, 4.8) * mm});
            skLineSegment(sketch, "E252", {"start": v(-2.77, 4.8) * mm, "end": v(-3.23, 5.53) * mm});
            skLineSegment(sketch, "E253", {"start": v(3.25, 5.53) * mm, "end": v(2.79, 4.8) * mm});
            skLineSegment(sketch, "E254", {"start": v(2.79, 4.8) * mm, "end": v(4.77, 3.88) * mm});
            skLineSegment(sketch, "E255", {"start": v(4.77, 3.88) * mm, "end": v(4.78, 3.87) * mm});
            skLineSegment(sketch, "E256", {"start": v(4.78, 3.87) * mm, "end": v(4.84, 3.85) * mm});
            skLineSegment(sketch, "E257", {"start": v(4.84, 3.85) * mm, "end": v(4.87, 3.86) * mm});
            skLineSegment(sketch, "E258", {"start": v(4.87, 3.86) * mm, "end": v(4.88, 3.86) * mm});
            skLineSegment(sketch, "E259", {"start": v(4.88, 3.86) * mm, "end": v(5.07, 4.2) * mm});
            skLineSegment(sketch, "E260", {"start": v(5.07, 4.2) * mm, "end": v(5.08, 4.2) * mm});
            skLineSegment(sketch, "E261", {"start": v(5.08, 4.2) * mm, "end": v(5.06, 4.24) * mm});
            skLineSegment(sketch, "E262", {"start": v(5.06, 4.24) * mm, "end": v(5.02, 4.28) * mm});
            skLineSegment(sketch, "E263", {"start": v(5.02, 4.28) * mm, "end": v(5, 4.3) * mm});
            skLineSegment(sketch, "E264", {"start": v(5, 4.3) * mm, "end": v(3.25, 5.53) * mm});
            skLineSegment(sketch, "E265", {"start": v(-3.65, 4.13) * mm, "end": v(-4.26, 3.84) * mm});
            skLineSegment(sketch, "E266", {"start": v(-4.26, 3.84) * mm, "end": v(-4.17, 3.72) * mm});
            skLineSegment(sketch, "E267", {"start": v(-4.17, 3.72) * mm, "end": v(-3.88, 3.37) * mm});
            skLineSegment(sketch, "E268", {"start": v(-3.88, 3.37) * mm, "end": v(-3.44, 2.94) * mm});
            skLineSegment(sketch, "E269", {"start": v(-3.44, 2.94) * mm, "end": v(-2.96, 2.56) * mm});
            skLineSegment(sketch, "E270", {"start": v(-2.96, 2.56) * mm, "end": v(-2.43, 2.25) * mm});
            skLineSegment(sketch, "E271", {"start": v(-2.43, 2.25) * mm, "end": v(-1.87, 2) * mm});
            skLineSegment(sketch, "E272", {"start": v(-1.87, 2) * mm, "end": v(-1.27, 1.8) * mm});
            skLineSegment(sketch, "E273", {"start": v(-1.27, 1.8) * mm, "end": v(-0.64, 1.69) * mm});
            skLineSegment(sketch, "E274", {"start": v(-0.64, 1.69) * mm, "end": v(-0.15, 1.65) * mm});
            skLineSegment(sketch, "E275", {"start": v(-0.15, 1.65) * mm, "end": v(0, 1.65) * mm});
            skLineSegment(sketch, "E276", {"start": v(0, 1.65) * mm, "end": v(0.17, 1.65) * mm});
            skLineSegment(sketch, "E277", {"start": v(0.17, 1.65) * mm, "end": v(0.66, 1.69) * mm});
            skLineSegment(sketch, "E278", {"start": v(0.66, 1.69) * mm, "end": v(1.28, 1.8) * mm});
            skLineSegment(sketch, "E279", {"start": v(1.28, 1.8) * mm, "end": v(1.88, 2) * mm});
            skLineSegment(sketch, "E280", {"start": v(1.88, 2) * mm, "end": v(2.44, 2.24) * mm});
            skLineSegment(sketch, "E281", {"start": v(2.44, 2.24) * mm, "end": v(2.97, 2.56) * mm});
            skLineSegment(sketch, "E282", {"start": v(2.97, 2.56) * mm, "end": v(3.45, 2.94) * mm});
            skLineSegment(sketch, "E283", {"start": v(3.45, 2.94) * mm, "end": v(3.9, 3.36) * mm});
            skLineSegment(sketch, "E284", {"start": v(3.9, 3.36) * mm, "end": v(4.19, 3.72) * mm});
            skLineSegment(sketch, "E285", {"start": v(4.19, 3.72) * mm, "end": v(4.28, 3.84) * mm});
            skLineSegment(sketch, "E286", {"start": v(4.28, 3.84) * mm, "end": v(3.66, 4.13) * mm});
            skLineSegment(sketch, "E287", {"start": v(3.66, 4.13) * mm, "end": v(3.58, 4.03) * mm});
            skLineSegment(sketch, "E288", {"start": v(3.58, 4.03) * mm, "end": v(3.33, 3.74) * mm});
            skLineSegment(sketch, "E289", {"start": v(3.33, 3.74) * mm, "end": v(2.95, 3.38) * mm});
            skLineSegment(sketch, "E290", {"start": v(2.95, 3.38) * mm, "end": v(2.53, 3.07) * mm});
            skLineSegment(sketch, "E291", {"start": v(2.53, 3.07) * mm, "end": v(2.08, 2.8) * mm});
            skLineSegment(sketch, "E292", {"start": v(2.08, 2.8) * mm, "end": v(1.6, 2.6) * mm});
            skLineSegment(sketch, "E293", {"start": v(1.6, 2.6) * mm, "end": v(1.1, 2.44) * mm});
            skLineSegment(sketch, "E294", {"start": v(1.1, 2.44) * mm, "end": v(0.56, 2.35) * mm});
            skLineSegment(sketch, "E295", {"start": v(0.56, 2.35) * mm, "end": v(0.15, 2.31) * mm});
            skLineSegment(sketch, "E296", {"start": v(0.15, 2.31) * mm, "end": v(0, 2.31) * mm});
            skLineSegment(sketch, "E297", {"start": v(0, 2.31) * mm, "end": v(-0.13, 2.31) * mm});
            skLineSegment(sketch, "E298", {"start": v(-0.13, 2.31) * mm, "end": v(-0.54, 2.35) * mm});
            skLineSegment(sketch, "E299", {"start": v(-0.54, 2.35) * mm, "end": v(-1.08, 2.44) * mm});
            skLineSegment(sketch, "E300", {"start": v(-1.08, 2.44) * mm, "end": v(-1.58, 2.6) * mm});
            skLineSegment(sketch, "E301", {"start": v(-1.58, 2.6) * mm, "end": v(-2.07, 2.8) * mm});
            skLineSegment(sketch, "E302", {"start": v(-2.07, 2.8) * mm, "end": v(-2.52, 3.07) * mm});
            skLineSegment(sketch, "E303", {"start": v(-2.52, 3.07) * mm, "end": v(-2.93, 3.38) * mm});
            skLineSegment(sketch, "E304", {"start": v(-2.93, 3.38) * mm, "end": v(-3.31, 3.74) * mm});
            skLineSegment(sketch, "E305", {"start": v(-3.31, 3.74) * mm, "end": v(-3.57, 4.03) * mm});
            skLineSegment(sketch, "E306", {"start": v(-3.57, 4.03) * mm, "end": v(-3.65, 4.13) * mm});
            skSolve(sketch);
        }
        {
            var Q0;
            Q0 = qSketchRegion(id + "F15", true);
            extrude(context, id + "F16", {"entities" : qUnion([Q0]), "operationType" : NewBodyOperationType.REMOVE, "oppositeDirection" : true, "depth" : .6 * mm, "offsetDistance" : 25 * mm});
        }
        {
            var Q0;
            Q0=makeQuery(id+"F6.boolean.opBoolean","INTERSECT",EDGE,{"derivedFrom":[makeQuery(id+"F1.opExtrude","SWEPT_FACE",FACE,{"disambiguationData":[OSD([sQuery(id+"F0.wireOp",EDGE,"E1")])]}),makeQuery(id+"F6.opExtrude","CAP_FACE",FACE,{"disambiguationData":[OSD([sQuery(id+"F5.wireOp",EDGE,"E9"),sQuery(id+"F5.wireOp",EDGE,"E10"),sQuery(id+"F5.wireOp",EDGE,"E11"),sQuery(id+"F5.wireOp",EDGE,"E12"),sQuery(id+"F5.wireOp",EDGE,"E13"),sQuery(id+"F5.wireOp",EDGE,"E14.filletArc"),sQuery(id+"F5.wireOp",EDGE,"E15.filletArc")])],"isStart":true})]});
            var Q1;
            Q1=makeQuery(id+"F6.boolean.opBoolean","INTERSECT",EDGE,{"derivedFrom":[makeQuery(id+"F1.opExtrude","SWEPT_FACE",FACE,{"disambiguationData":[OSD([sQuery(id+"F0.wireOp",EDGE,"E1")])]}),makeQuery(id+"F6.opExtrude","CAP_FACE",FACE,{"disambiguationData":[OSD([sQuery(id+"F5.wireOp",EDGE,"E9"),sQuery(id+"F5.wireOp",EDGE,"E10"),sQuery(id+"F5.wireOp",EDGE,"E11"),sQuery(id+"F5.wireOp",EDGE,"E12"),sQuery(id+"F5.wireOp",EDGE,"E13"),sQuery(id+"F5.wireOp",EDGE,"E14.filletArc"),sQuery(id+"F5.wireOp",EDGE,"E15.filletArc")])],"isStart":false})]});
            var Q2;
            Q2=makeQuery(id+"F12.opBoolean","INTERSECT",EDGE,{"derivedFrom":[makeQuery(id+"F1.opExtrude","SWEPT_FACE",FACE,{"disambiguationData":[OSD([sQuery(id+"F0.wireOp",EDGE,"E1")])]}),makeQuery(id+"F3.opExtrude","CAP_FACE",FACE,{"disambiguationData":[OSD([sQuery(id+"F2.wireOp",EDGE,"E2"),sQuery(id+"F2.wireOp",EDGE,"E4"),sQuery(id+"F2.wireOp",EDGE,"E5"),sQuery(id+"F2.wireOp",EDGE,"E6"),sQuery(id+"F2.wireOp",EDGE,"E7"),sQuery(id+"F2.wireOp",EDGE,"E8")])],"isStart":false})]});
            var Q3;
            Q3=makeQuery(id+"F12.opBoolean","INTERSECT",EDGE,{"derivedFrom":[makeQuery(id+"F1.opExtrude","SWEPT_FACE",FACE,{"disambiguationData":[OSD([sQuery(id+"F0.wireOp",EDGE,"E0")])]}),makeQuery(id+"F3.opExtrude","CAP_FACE",FACE,{"disambiguationData":[OSD([sQuery(id+"F2.wireOp",EDGE,"E2"),sQuery(id+"F2.wireOp",EDGE,"E4"),sQuery(id+"F2.wireOp",EDGE,"E5"),sQuery(id+"F2.wireOp",EDGE,"E6"),sQuery(id+"F2.wireOp",EDGE,"E7"),sQuery(id+"F2.wireOp",EDGE,"E8")])],"isStart":false})]});
            var Q4;
            Q4=makeQuery(id+"F9.boolean.opBoolean","INTERSECT",EDGE,{"derivedFrom":[makeQuery(id+"F1.opExtrude","SWEPT_FACE",FACE,{"disambiguationData":[OSD([sQuery(id+"F0.wireOp",EDGE,"E0")])]}),makeQuery(id+"F9.opExtrude","CAP_FACE",FACE,{"disambiguationData":[OSD([sQuery(id+"F8.wireOp",EDGE,"E16"),sQuery(id+"F8.wireOp",EDGE,"E17"),sQuery(id+"F8.wireOp",EDGE,"E18"),sQuery(id+"F8.wireOp",EDGE,"E19"),sQuery(id+"F8.wireOp",EDGE,"E20"),sQuery(id+"F8.wireOp",EDGE,"E21.filletArc"),sQuery(id+"F8.wireOp",EDGE,"E22.filletArc")])],"isStart":false})]});
            var Q5;
            Q5=makeQuery(id+"F9.boolean.opBoolean","INTERSECT",EDGE,{"derivedFrom":[makeQuery(id+"F1.opExtrude","SWEPT_FACE",FACE,{"disambiguationData":[OSD([sQuery(id+"F0.wireOp",EDGE,"E0")])]}),makeQuery(id+"F9.opExtrude","CAP_FACE",FACE,{"disambiguationData":[OSD([sQuery(id+"F8.wireOp",EDGE,"E16"),sQuery(id+"F8.wireOp",EDGE,"E17"),sQuery(id+"F8.wireOp",EDGE,"E18"),sQuery(id+"F8.wireOp",EDGE,"E19"),sQuery(id+"F8.wireOp",EDGE,"E20"),sQuery(id+"F8.wireOp",EDGE,"E21.filletArc"),sQuery(id+"F8.wireOp",EDGE,"E22.filletArc")])],"isStart":true})]});
            fillet(context, id + "F17", {"entities" : qUnion([Q0, Q1, Q2, Q3, Q4, Q5]), "radius" : 2 * mm, "tangentPropagation" : true, "allowEdgeOverflow" : false});
        }
    });
